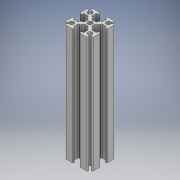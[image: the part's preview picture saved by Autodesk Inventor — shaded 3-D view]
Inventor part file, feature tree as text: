
AUTODESK INVENTOR PART (.ipt)
format: ipt  version: 2018.3 (Build 223284000, 284)  size: 740,864 bytes
history: native  units: mm
features: sketch x4, extrude x4, projected_geometry x4, plane x1, fillet x1
ambient origin geometry x8: Origin, YZ Plane, XZ Plane, XY Plane, X Axis, Y Axis, Z Axis, Center Point
bodies: Solid1 (feature_tree)
feature tree (14):
  sketch  "Sketch1"  dims[d0=10.0mm d1=0.0mm d2=165.1mm d3=0.0mm]
  plane  "Work Plane1"
  extrude  "Extrusion1"  Depth=165.1mm TaperAngle=0.0deg
  sketch  "Sketch2"  dims[d4=228.6mm d5=0.0mm d6=12.7mm d7=0.0mm]
  extrude  "Extrusion2"  Depth=12.7mm TaperAngle=0.0deg
  extrude  "Extrusion3"  [1 undecoded]
  extrude  "Extrusion4"  [1 undecoded]
  projected_geometry  "Projected Loop1"
  projected_geometry  "Projected Loop2"
  sketch  "Sketch3"
  projected_geometry  "Projected Loop3"
  sketch  "Sketch4"
  projected_geometry  "Projected Loop4"
  fillet  "Fillet6"  [1 undecoded]
note: 3 required parameter values undecoded (feature->parameter linkage not recoverable at this tier; creation-order binding heuristic only, values carry confidence <= 0.55)
